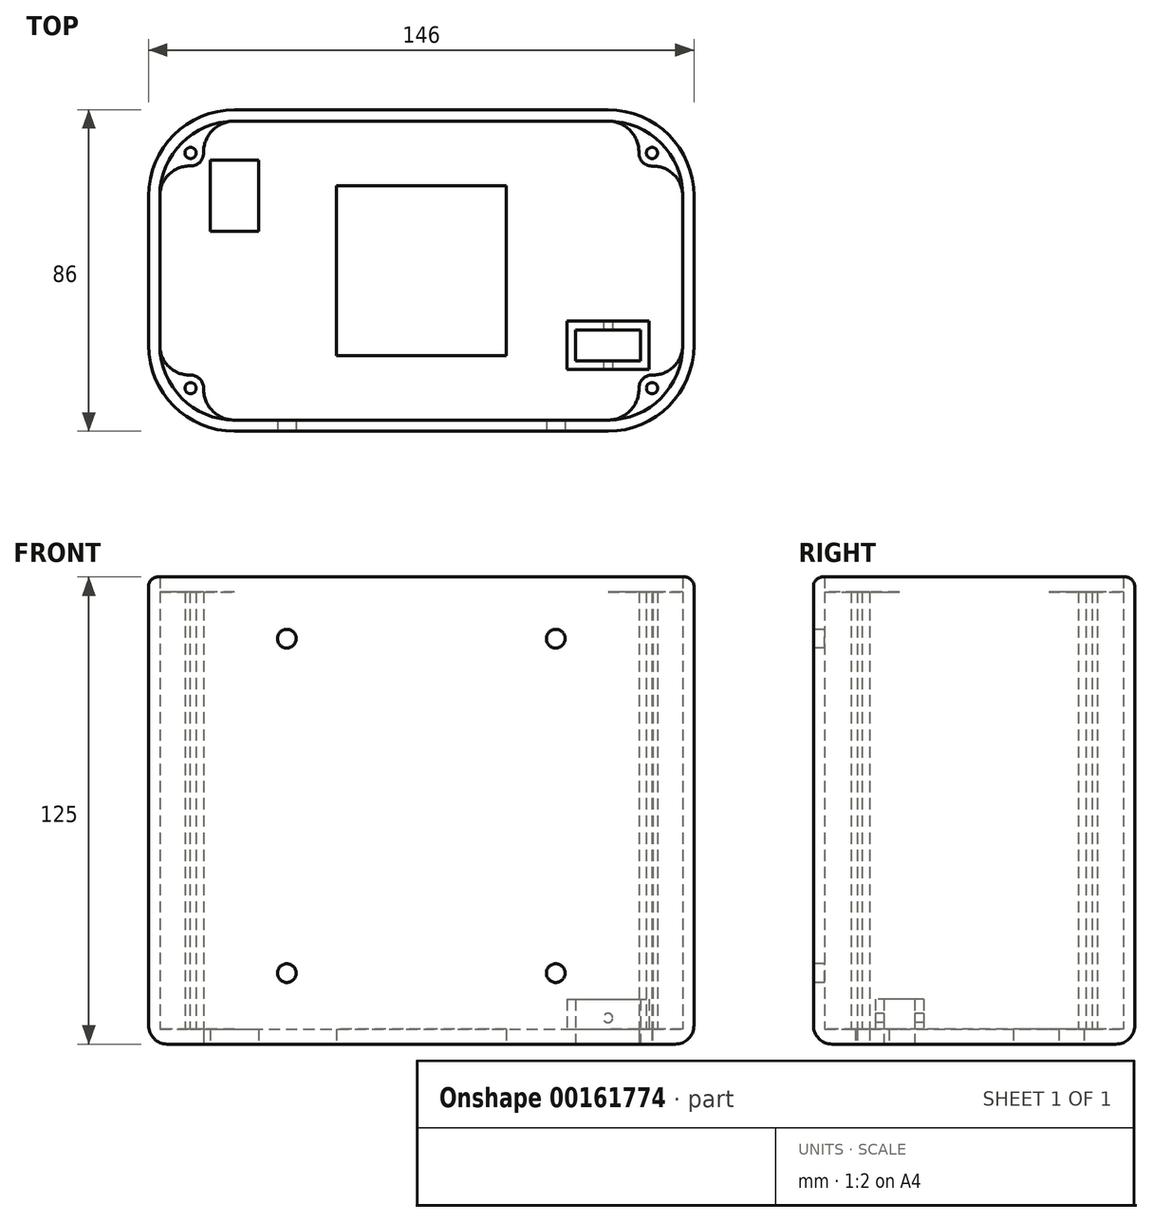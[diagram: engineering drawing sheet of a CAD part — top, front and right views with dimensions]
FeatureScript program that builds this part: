
annotation { "Feature Type Name" : "Feature", "Feature Type Description" : "" }
export const myFeature = defineFeature(function(context is Context, id is Id, definition is map)
    precondition{}
    {
        {
            var Q0;
            Q0=qCreatedBy(makeId("Top.planeOp"),FACE);
            var sketch = newSketch(context, id + "F0", { "sketchPlane" : qUnion([Q0])});
            skPoint(sketch, "E0.middle", {"position": v(5.38, 0.07) * mm});
            skLineSegment(sketch, "E1.left", {"start": v(24.9, 0.52) * mm, "end": v(24.9, -0.25) * mm});
            skLineSegment(sketch, "E2.left", {"start": v(-14.1, 0.52) * mm, "end": v(-14.1, -0.25) * mm});
            skPoint(sketch, "E3.visualSharp", {"position": v(-64.62, 30.07) * mm});
            skPoint(sketch, "E4.visualSharp", {"position": v(75.38, 30.07) * mm});
            skPoint(sketch, "E5.visualSharp", {"position": v(75.38, -29.93) * mm});
            skPoint(sketch, "E6.visualSharp", {"position": v(-64.62, -29.93) * mm});
            skLineSegment(sketch, "E7.bottom", {"start": v(55.38, 40.07) * mm, "end": v(-44.62, 40.07) * mm});
            skLineSegment(sketch, "E7.top", {"start": v(55.38, -39.93) * mm, "end": v(-44.62, -39.93) * mm});
            skLineSegment(sketch, "E7.left", {"start": v(75.38, 20.07) * mm, "end": v(75.38, -19.93) * mm});
            skLineSegment(sketch, "E7.right", {"start": v(-64.62, 20.07) * mm, "end": v(-64.62, -19.93) * mm});
            skPoint(sketch, "E8.visualSharp", {"position": v(-64.62, 40.07) * mm});
            skArc(sketch, "E8.filletArc", {"start": v(-44.62, 40.07) * mm, "mid": v(-58.77, 34.2) * mm, "end": v(-64.62, 20.07) * mm});
            skPoint(sketch, "E9.visualSharp", {"position": v(75.38, 40.07) * mm});
            skArc(sketch, "E9.filletArc", {"start": v(75.38, 20.07) * mm, "mid": v(69.52, 34.2) * mm, "end": v(55.38, 40.07) * mm});
            skPoint(sketch, "E10.visualSharp", {"position": v(75.38, -39.93) * mm});
            skArc(sketch, "E10.filletArc", {"start": v(55.38, -39.93) * mm, "mid": v(69.52, -34.08) * mm, "end": v(75.38, -19.93) * mm});
            skPoint(sketch, "E11.visualSharp", {"position": v(-64.62, -39.93) * mm});
            skArc(sketch, "E11.filletArc", {"start": v(-64.62, -19.93) * mm, "mid": v(-58.77, -34.08) * mm, "end": v(-44.62, -39.93) * mm});
            skLineSegment(sketch, "E12.bottom", {"start": v(-44.62, 44.07) * mm, "end": v(55.38, 44.07) * mm});
            skLineSegment(sketch, "E12.top", {"start": v(-44.62, -43.93) * mm, "end": v(55.38, -43.93) * mm});
            skLineSegment(sketch, "E12.left", {"start": v(-68.62, 20.07) * mm, "end": v(-68.62, -19.93) * mm});
            skLineSegment(sketch, "E12.right", {"start": v(79.38, 20.07) * mm, "end": v(79.38, -19.93) * mm});
            skPoint(sketch, "E13.visualSharp", {"position": v(-68.62, 44.07) * mm});
            skArc(sketch, "E13.filletArc", {"start": v(-44.62, 44.07) * mm, "mid": v(-61.6, 37.04) * mm, "end": v(-68.62, 20.07) * mm});
            skPoint(sketch, "E14.visualSharp", {"position": v(79.38, 44.07) * mm});
            skArc(sketch, "E14.filletArc", {"start": v(79.38, 20.07) * mm, "mid": v(72.35, 37.04) * mm, "end": v(55.38, 44.07) * mm});
            skPoint(sketch, "E15.visualSharp", {"position": v(79.38, -43.93) * mm});
            skArc(sketch, "E15.filletArc", {"start": v(55.38, -43.93) * mm, "mid": v(72.35, -36.9) * mm, "end": v(79.38, -19.93) * mm});
            skPoint(sketch, "E16.visualSharp", {"position": v(-68.62, -43.93) * mm});
            skArc(sketch, "E16.filletArc", {"start": v(-68.62, -19.93) * mm, "mid": v(-61.6, -36.9) * mm, "end": v(-44.62, -43.93) * mm});
            skLineSegment(sketch, "E17.bottom", {"start": v(28.13, 22.82) * mm, "end": v(-17.37, 22.82) * mm});
            skLineSegment(sketch, "E17.top", {"start": v(28.13, -22.68) * mm, "end": v(-17.37, -22.68) * mm});
            skLineSegment(sketch, "E17.left", {"start": v(28.13, 22.82) * mm, "end": v(28.13, -22.68) * mm});
            skLineSegment(sketch, "E17.right", {"start": v(-17.37, 22.82) * mm, "end": v(-17.37, -22.68) * mm});
            skCircle(sketch, "E18", {"center": v(67.15, 31.53) * mm, "radius": 3.5 * mm});
            skCircle(sketch, "E19", {"center": v(67.15, 31.53) * mm, "radius": 1.5 * mm});
            skCircle(sketch, "E20", {"center": v(-56.4, 31.53) * mm, "radius": 3.5 * mm});
            skCircle(sketch, "E21", {"center": v(-56.4, 31.53) * mm, "radius": 1.5 * mm});
            skCircle(sketch, "E22", {"center": v(-56.4, -31.4) * mm, "radius": 3.5 * mm});
            skCircle(sketch, "E23", {"center": v(-56.4, -31.4) * mm, "radius": 1.5 * mm});
            skCircle(sketch, "E24", {"center": v(67.16, -31.4) * mm, "radius": 3.5 * mm});
            skCircle(sketch, "E25", {"center": v(67.16, -31.4) * mm, "radius": 1.5 * mm});
            skLineSegment(sketch, "E26.bottom", {"start": v(48.88, 29.57) * mm, "end": v(61.88, 29.57) * mm});
            skLineSegment(sketch, "E26.top", {"start": v(48.88, 10.57) * mm, "end": v(61.88, 10.57) * mm});
            skLineSegment(sketch, "E26.left", {"start": v(48.88, 29.57) * mm, "end": v(48.88, 10.57) * mm});
            skLineSegment(sketch, "E26.right", {"start": v(61.88, 29.57) * mm, "end": v(61.88, 10.57) * mm});
            skLineSegment(sketch, "E27.bottom", {"start": v(-35.97, -15.78) * mm, "end": v(-53.27, -15.78) * mm});
            skLineSegment(sketch, "E27.top", {"start": v(-35.97, -24.08) * mm, "end": v(-53.27, -24.08) * mm});
            skLineSegment(sketch, "E27.left", {"start": v(-35.97, -15.78) * mm, "end": v(-35.97, -24.08) * mm});
            skLineSegment(sketch, "E27.right", {"start": v(-53.27, -15.78) * mm, "end": v(-53.27, -24.08) * mm});
            skLineSegment(sketch, "E28.bottom", {"start": v(-33.62, -13.43) * mm, "end": v(-55.62, -13.43) * mm});
            skLineSegment(sketch, "E28.top", {"start": v(-33.62, -26.43) * mm, "end": v(-55.62, -26.43) * mm});
            skLineSegment(sketch, "E28.left", {"start": v(-33.62, -13.43) * mm, "end": v(-33.62, -26.43) * mm});
            skLineSegment(sketch, "E28.right", {"start": v(-55.62, -13.43) * mm, "end": v(-55.62, -26.43) * mm});
            skArc(sketch, "E29", {"start": v(75.38, 20.07) * mm, "mid": v(73.03, 25.72) * mm, "end": v(67.36, 28.03) * mm});
            skArc(sketch, "E30", {"start": v(55.38, 40.07) * mm, "mid": v(61.29, 37.58) * mm, "end": v(63.65, 31.62) * mm});
            skArc(sketch, "E31", {"start": v(55.38, -39.93) * mm, "mid": v(61.38, -37.36) * mm, "end": v(63.66, -31.23) * mm});
            skArc(sketch, "E32", {"start": v(67.18, -27.9) * mm, "mid": v(72.96, -25.65) * mm, "end": v(75.38, -19.93) * mm});
            skArc(sketch, "E33", {"start": v(-52.9, -31.22) * mm, "mid": v(-50.63, -37.35) * mm, "end": v(-44.62, -39.93) * mm});
            skArc(sketch, "E34", {"start": v(-64.62, -19.93) * mm, "mid": v(-62.22, -25.63) * mm, "end": v(-56.47, -27.9) * mm});
            skArc(sketch, "E35", {"start": v(-56.64, 28.04) * mm, "mid": v(-62.28, 25.71) * mm, "end": v(-64.62, 20.07) * mm});
            skArc(sketch, "E36", {"start": v(-44.62, 40.07) * mm, "mid": v(-50.52, 37.6) * mm, "end": v(-52.9, 31.67) * mm});
            skLineSegment(sketch, "E37.bottom", {"start": v(-51.12, 29.57) * mm, "end": v(-38.12, 29.57) * mm});
            skLineSegment(sketch, "E37.top", {"start": v(-51.12, 10.57) * mm, "end": v(-38.12, 10.57) * mm});
            skLineSegment(sketch, "E37.left", {"start": v(-51.12, 29.57) * mm, "end": v(-51.12, 10.57) * mm});
            skLineSegment(sketch, "E37.right", {"start": v(-38.12, 29.57) * mm, "end": v(-38.12, 10.57) * mm});
            skLineSegment(sketch, "E38.bottom", {"start": v(46.73, -15.78) * mm, "end": v(64.03, -15.78) * mm});
            skLineSegment(sketch, "E38.top", {"start": v(46.73, -24.08) * mm, "end": v(64.03, -24.08) * mm});
            skLineSegment(sketch, "E38.left", {"start": v(46.73, -15.78) * mm, "end": v(46.73, -24.08) * mm});
            skLineSegment(sketch, "E38.right", {"start": v(64.03, -15.78) * mm, "end": v(64.03, -24.08) * mm});
            skLineSegment(sketch, "E39.bottom", {"start": v(44.38, -13.43) * mm, "end": v(66.38, -13.43) * mm});
            skLineSegment(sketch, "E39.top", {"start": v(44.38, -26.43) * mm, "end": v(66.38, -26.43) * mm});
            skLineSegment(sketch, "E39.left", {"start": v(44.38, -13.43) * mm, "end": v(44.38, -26.43) * mm});
            skLineSegment(sketch, "E39.right", {"start": v(66.38, -13.43) * mm, "end": v(66.38, -26.43) * mm});
            skArc(sketch, "E40.0", {"start": v(78.38, 20.07) * mm, "mid": v(71.64, 36.33) * mm, "end": v(55.38, 43.07) * mm});
            skLineSegment(sketch, "E40.1", {"start": v(78.38, 20.07) * mm, "end": v(78.38, -19.93) * mm});
            skLineSegment(sketch, "E40.2", {"start": v(55.38, 43.07) * mm, "end": v(-44.62, 43.07) * mm});
            skArc(sketch, "E40.3", {"start": v(55.38, -42.93) * mm, "mid": v(71.64, -36.2) * mm, "end": v(78.38, -19.93) * mm});
            skArc(sketch, "E40.4", {"start": v(-44.62, 43.07) * mm, "mid": v(-60.89, 36.33) * mm, "end": v(-67.62, 20.07) * mm});
            skLineSegment(sketch, "E40.5", {"start": v(-67.62, 20.07) * mm, "end": v(-67.62, -19.93) * mm});
            skArc(sketch, "E40.6", {"start": v(-67.62, -19.93) * mm, "mid": v(-60.89, -36.2) * mm, "end": v(-44.62, -42.93) * mm});
            skLineSegment(sketch, "E40.7", {"start": v(55.38, -42.93) * mm, "end": v(-44.62, -42.93) * mm});
            skSolve(sketch);
        }
        {
            var Q0;
            Q0=makeQuery(id+"F0.imprint","IMPRINT",FACE,{"disambiguationData":[TD([[makeQuery(id+"F0.imprint","IMPRINT",EDGE,{"derivedFrom":sQuery(id+"F0.wireOp",EDGE,"E7.bottom")}),1.0]])]});
            var Q1;
            Q1=makeQuery(id+"F0.imprint","IMPRINT",FACE,{"disambiguationData":[TD([[makeQuery(id+"F0.imprint","IMPRINT",EDGE,{"derivedFrom":sQuery(id+"F0.wireOp",EDGE,"E18")}),1.0]])]});
            var Q2;
            Q2=makeQuery(id+"F0.imprint","IMPRINT",FACE,{"disambiguationData":[TD([[makeQuery(id+"F0.imprint","IMPRINT",EDGE,{"derivedFrom":sQuery(id+"F0.wireOp",EDGE,"E19")}),1.0]])]});
            var Q3;
            Q3=makeQuery(id+"F0.imprint","IMPRINT",FACE,{"disambiguationData":[TD([[makeQuery(id+"F0.imprint","IMPRINT",EDGE,{"derivedFrom":sQuery(id+"F0.wireOp",EDGE,"E24")}),1.0]])]});
            var Q4;
            Q4=makeQuery(id+"F0.imprint","IMPRINT",FACE,{"disambiguationData":[TD([[makeQuery(id+"F0.imprint","IMPRINT",EDGE,{"derivedFrom":sQuery(id+"F0.wireOp",EDGE,"E25")}),1.0]])]});
            var Q5;
            Q5=makeQuery(id+"F0.imprint","IMPRINT",FACE,{"disambiguationData":[TD([[makeQuery(id+"F0.imprint","IMPRINT",EDGE,{"derivedFrom":sQuery(id+"F0.wireOp",EDGE,"E22")}),1.0]])]});
            var Q6;
            Q6=makeQuery(id+"F0.imprint","IMPRINT",FACE,{"disambiguationData":[TD([[makeQuery(id+"F0.imprint","IMPRINT",EDGE,{"derivedFrom":sQuery(id+"F0.wireOp",EDGE,"E23")}),1.0]])]});
            var Q7;
            Q7=makeQuery(id+"F0.imprint","IMPRINT",FACE,{"disambiguationData":[TD([[makeQuery(id+"F0.imprint","IMPRINT",EDGE,{"derivedFrom":sQuery(id+"F0.wireOp",EDGE,"E20")}),1.0]])]});
            var Q8;
            Q8=makeQuery(id+"F0.imprint","IMPRINT",FACE,{"disambiguationData":[TD([[makeQuery(id+"F0.imprint","IMPRINT",EDGE,{"derivedFrom":sQuery(id+"F0.wireOp",EDGE,"E21")}),1.0]])]});
            var Q9;
            Q9=makeQuery(id+"F0.imprint","IMPRINT",FACE,{"disambiguationData":[TD([[makeQuery(id+"F0.imprint","IMPRINT",EDGE,{"derivedFrom":sQuery(id+"F0.wireOp",EDGE,"E7.bottom")}),-1.0]])]});
            var Q10;
            Q10=makeQuery(id+"F0.imprint","IMPRINT",FACE,{"disambiguationData":[TD([[makeQuery(id+"F0.imprint","IMPRINT",EDGE,{"derivedFrom":sQuery(id+"F0.wireOp",EDGE,"E8.filletArc")}),1.0]])]});
            var Q11;
            Q11=makeQuery(id+"F0.imprint","IMPRINT",FACE,{"disambiguationData":[TD([[makeQuery(id+"F0.imprint","IMPRINT",EDGE,{"derivedFrom":sQuery(id+"F0.wireOp",EDGE,"E9.filletArc")}),1.0]])]});
            var Q12;
            {var subQ0=sQuery(id+"F0.wireOp",EDGE,"E10.filletArc");Q12=makeQuery(id+"F0.imprint","IMPRINT",FACE,{"disambiguationData":[TD([[makeQuery(id+"F0.imprint","IMPRINT",EDGE,{"derivedFrom":subQ0}),1.0]])]});}
            var Q13;
            {var subQ0=sQuery(id+"F0.wireOp",EDGE,"E11.filletArc");Q13=makeQuery(id+"F0.imprint","IMPRINT",FACE,{"disambiguationData":[TD([[makeQuery(id+"F0.imprint","IMPRINT",EDGE,{"derivedFrom":subQ0}),1.0]])]});}
            var Q14;
            Q14=makeQuery(id+"F0.imprint","IMPRINT",FACE,{"disambiguationData":[TD([[makeQuery(id+"F0.imprint","IMPRINT",EDGE,{"derivedFrom":sQuery(id+"F0.wireOp",EDGE,"E26.bottom")}),-1.0]])]});
            var Q15;
            Q15=makeQuery(id+"F0.imprint","IMPRINT",FACE,{"disambiguationData":[TD([[makeQuery(id+"F0.imprint","IMPRINT",EDGE,{"derivedFrom":sQuery(id+"F0.wireOp",EDGE,"E27.bottom")}),-1.0]])]});
            var Q16;
            Q16=makeQuery(id+"F0.imprint","IMPRINT",FACE,{"disambiguationData":[TD([[makeQuery(id+"F0.imprint","IMPRINT",EDGE,{"derivedFrom":sQuery(id+"F0.wireOp",EDGE,"E27.bottom")}),1.0]])]});
            extrude(context, id + "F1", {"entities" : qUnion([Q0, Q1, Q2, Q3, Q4, Q5, Q6, Q7, Q8, Q9, Q10, Q11, Q12, Q13, Q14, Q15, Q16]), "depth" : 4 * mm});
        }
        {
            var Q0;
            Q0=makeQuery(id+"F0.imprint","IMPRINT",FACE,{"disambiguationData":[TD([[makeQuery(id+"F0.imprint","IMPRINT",EDGE,{"derivedFrom":sQuery(id+"F0.wireOp",EDGE,"E38.bottom")}),1.0]])]});
            extrude(context, id + "F2", {"entities" : qUnion([Q0]), "operationType" : NewBodyOperationType.ADD, "depth" : 12 * mm});
        }
        {
            var Q0;
            Q0=makeQuery(id+"F0.imprint","IMPRINT",FACE,{"disambiguationData":[TD([[makeQuery(id+"F0.imprint","IMPRINT",EDGE,{"derivedFrom":sQuery(id+"F0.wireOp",EDGE,"E8.filletArc")}),1.0]])]});
            var Q1;
            Q1=makeQuery(id+"F0.imprint","IMPRINT",FACE,{"disambiguationData":[TD([[makeQuery(id+"F0.imprint","IMPRINT",EDGE,{"derivedFrom":sQuery(id+"F0.wireOp",EDGE,"E21")}),-1.0]])]});
            var Q2;
            {var subQ0=sQuery(id+"F0.wireOp",EDGE,"E11.filletArc");Q2=makeQuery(id+"F0.imprint","IMPRINT",FACE,{"disambiguationData":[TD([[makeQuery(id+"F0.imprint","IMPRINT",EDGE,{"derivedFrom":subQ0}),1.0]])]});}
            var Q3;
            Q3=makeQuery(id+"F0.imprint","IMPRINT",FACE,{"disambiguationData":[TD([[makeQuery(id+"F0.imprint","IMPRINT",EDGE,{"derivedFrom":sQuery(id+"F0.wireOp",EDGE,"E23")}),-1.0]])]});
            var Q4;
            {var subQ0=sQuery(id+"F0.wireOp",EDGE,"E10.filletArc");Q4=makeQuery(id+"F0.imprint","IMPRINT",FACE,{"disambiguationData":[TD([[makeQuery(id+"F0.imprint","IMPRINT",EDGE,{"derivedFrom":subQ0}),1.0]])]});}
            var Q5;
            Q5=makeQuery(id+"F0.imprint","IMPRINT",FACE,{"disambiguationData":[TD([[makeQuery(id+"F0.imprint","IMPRINT",EDGE,{"derivedFrom":sQuery(id+"F0.wireOp",EDGE,"E25")}),-1.0]])]});
            var Q6;
            Q6=makeQuery(id+"F0.imprint","IMPRINT",FACE,{"disambiguationData":[TD([[makeQuery(id+"F0.imprint","IMPRINT",EDGE,{"derivedFrom":sQuery(id+"F0.wireOp",EDGE,"E9.filletArc")}),1.0]])]});
            var Q7;
            Q7=makeQuery(id+"F0.imprint","IMPRINT",FACE,{"disambiguationData":[TD([[makeQuery(id+"F0.imprint","IMPRINT",EDGE,{"derivedFrom":sQuery(id+"F0.wireOp",EDGE,"E19")}),-1.0]])]});
            extrude(context, id + "F3", {"entities" : qUnion([Q0, Q1, Q2, Q3, Q4, Q5, Q6, Q7]), "operationType" : NewBodyOperationType.ADD, "depth" : 121 * mm});
        }
        {
            var Q0;
            Q0=makeQuery(id+"F0.imprint","IMPRINT",FACE,{"disambiguationData":[TD([[makeQuery(id+"F0.imprint","IMPRINT",EDGE,{"derivedFrom":sQuery(id+"F0.wireOp",EDGE,"E7.bottom")}),-1.0]])]});
            extrude(context, id + "F4", {"entities" : qUnion([Q0]), "operationType" : NewBodyOperationType.ADD, "depth" : 125 * mm});
        }
        {
            var Q0;
            Q0=makeQuery(id+"F1.opExtrude","CAP_EDGE",EDGE,{"disambiguationData":[OSD([sQuery(id+"F0.wireOp",EDGE,"E40.2")])],"isStart":true});
            fillet(context, id + "F5", {"entities" : qUnion([Q0]), "radius" : 5 * mm, "tangentPropagation" : true, "allowEdgeOverflow" : false});
        }
        {
            var Q0;
            Q0=makeQuery(id+"F4.opExtrude","CAP_EDGE",EDGE,{"disambiguationData":[OSD([sQuery(id+"F0.wireOp",EDGE,"E40.2")])],"isStart":false});
            fillet(context, id + "F6", {"entities" : qUnion([Q0]), "radius" : 2.5 * mm, "tangentPropagation" : true, "allowEdgeOverflow" : false});
        }
        {
            var Q0;
            Q0=makeQuery(id+"F2.opExtrude","SWEPT_FACE",FACE,{"disambiguationData":[OSD([sQuery(id+"F0.wireOp",EDGE,"E38.top")])]});
            var sketch = newSketch(context, id + "F7", { "sketchPlane" : qUnion([Q0])});
            skLineSegment(sketch, "E41", {"start": v(-55.38, 0) * mm, "end": v(-55.38, 7) * mm});
            skCircle(sketch, "E42", {"center": v(-55.38, 7) * mm, "radius": 1.25 * mm});
            skSolve(sketch);
        }
        {
            var Q0;
            Q0=makeQuery(id+"F7.imprint","IMPRINT",FACE,{"disambiguationData":[TD([[makeQuery(id+"F7.imprint","IMPRINT",EDGE,{"derivedFrom":sQuery(id+"F7.wireOp",EDGE,"E42")}),1.0]])]});
            extrude(context, id + "F8", {"entities" : qUnion([Q0]), "operationType" : NewBodyOperationType.REMOVE, "endBound" : BoundingType.SYMMETRIC, "depth" : 30 * mm});
        }
        {
            var Q0;
            {var subQ0=sQuery(id+"F0.wireOp",EDGE,"E40.7");Q0=makeQuery(id+"F4.boolean.opBoolean","MERGE",FACE,{"derivedFrom":[makeQuery(id+"F1.opExtrude","SWEPT_FACE",FACE,{"disambiguationData":[OSD([subQ0])]}),makeQuery(id+"F4.opExtrude","SWEPT_FACE",FACE,{"disambiguationData":[OSD([subQ0])]})]});}
            var sketch = newSketch(context, id + "F9", { "sketchPlane" : qUnion([Q0])});
            skLineSegment(sketch, "E43.bottom", {"start": v(-44.62, 122.5) * mm, "end": v(-30.62, 122.5) * mm});
            skLineSegment(sketch, "E43.top", {"start": v(-44.62, 108.5) * mm, "end": v(-30.62, 108.5) * mm});
            skLineSegment(sketch, "E43.left", {"start": v(-44.62, 122.5) * mm, "end": v(-44.62, 108.5) * mm});
            skLineSegment(sketch, "E43.right", {"start": v(-30.62, 122.5) * mm, "end": v(-30.62, 108.5) * mm});
            skLineSegment(sketch, "E44.bottom", {"start": v(-44.62, 5) * mm, "end": v(-30.62, 5) * mm});
            skLineSegment(sketch, "E44.top", {"start": v(-44.62, 19) * mm, "end": v(-30.62, 19) * mm});
            skLineSegment(sketch, "E44.left", {"start": v(-44.62, 5) * mm, "end": v(-44.62, 19) * mm});
            skLineSegment(sketch, "E44.right", {"start": v(-30.62, 5) * mm, "end": v(-30.62, 19) * mm});
            skLineSegment(sketch, "E45.bottom", {"start": v(55.38, 5) * mm, "end": v(41.38, 5) * mm});
            skLineSegment(sketch, "E45.top", {"start": v(55.38, 19) * mm, "end": v(41.38, 19) * mm});
            skLineSegment(sketch, "E45.left", {"start": v(55.38, 5) * mm, "end": v(55.38, 19) * mm});
            skLineSegment(sketch, "E45.right", {"start": v(41.38, 5) * mm, "end": v(41.38, 19) * mm});
            skLineSegment(sketch, "E46.bottom", {"start": v(55.38, 122.5) * mm, "end": v(41.38, 122.5) * mm});
            skLineSegment(sketch, "E46.top", {"start": v(55.38, 108.5) * mm, "end": v(41.38, 108.5) * mm});
            skLineSegment(sketch, "E46.left", {"start": v(55.38, 122.5) * mm, "end": v(55.38, 108.5) * mm});
            skLineSegment(sketch, "E46.right", {"start": v(41.38, 122.5) * mm, "end": v(41.38, 108.5) * mm});
            skCircle(sketch, "E47", {"center": v(-30.62, 108.5) * mm, "radius": 2.5 * mm});
            skCircle(sketch, "E48", {"center": v(41.38, 108.5) * mm, "radius": 2.5 * mm});
            skCircle(sketch, "E49", {"center": v(-30.62, 19) * mm, "radius": 2.5 * mm});
            skCircle(sketch, "E50", {"center": v(41.38, 19) * mm, "radius": 2.5 * mm});
            skSolve(sketch);
        }
        {
            var Q0;
            {var subQ0=sQuery(id+"F9.wireOp",EDGE,"E43.right");var subQ1=sQuery(id+"F9.wireOp",EDGE,"E43.top");var subQ2=makeQuery(id+"F9.imprint","INTERSECT",VERTEX,{"derivedFrom":[subQ1,subQ0]});Q0=makeQuery(id+"F9.imprint","IMPRINT",FACE,{"disambiguationData":[TD([[makeQuery(id+"F9.imprint","IMPRINT",EDGE,{"disambiguationData":[TD([[subQ2,1.0]])],"derivedFrom":subQ1}),1.0]])]});}
            var Q1;
            {var subQ0=sQuery(id+"F9.wireOp",EDGE,"E43.right");var subQ1=sQuery(id+"F9.wireOp",EDGE,"E43.top");var subQ2=makeQuery(id+"F9.imprint","INTERSECT",VERTEX,{"derivedFrom":[subQ1,subQ0]});Q1=makeQuery(id+"F9.imprint","IMPRINT",FACE,{"disambiguationData":[TD([[makeQuery(id+"F9.imprint","IMPRINT",EDGE,{"disambiguationData":[TD([[subQ2,1.0]])],"derivedFrom":subQ1}),-1.0]])]});}
            var Q2;
            {var subQ0=sQuery(id+"F9.wireOp",EDGE,"E44.right");var subQ1=sQuery(id+"F9.wireOp",EDGE,"E44.top");var subQ2=makeQuery(id+"F9.imprint","INTERSECT",VERTEX,{"derivedFrom":[subQ1,subQ0]});Q2=makeQuery(id+"F9.imprint","IMPRINT",FACE,{"disambiguationData":[TD([[makeQuery(id+"F9.imprint","IMPRINT",EDGE,{"disambiguationData":[TD([[subQ2,1.0]])],"derivedFrom":subQ1}),-1.0]])]});}
            var Q3;
            {var subQ0=sQuery(id+"F9.wireOp",EDGE,"E44.right");var subQ1=sQuery(id+"F9.wireOp",EDGE,"E44.top");var subQ2=makeQuery(id+"F9.imprint","INTERSECT",VERTEX,{"derivedFrom":[subQ1,subQ0]});Q3=makeQuery(id+"F9.imprint","IMPRINT",FACE,{"disambiguationData":[TD([[makeQuery(id+"F9.imprint","IMPRINT",EDGE,{"disambiguationData":[TD([[subQ2,1.0]])],"derivedFrom":subQ1}),1.0]])]});}
            var Q4;
            {var subQ0=sQuery(id+"F9.wireOp",EDGE,"E45.right");var subQ1=sQuery(id+"F9.wireOp",EDGE,"E45.top");var subQ2=makeQuery(id+"F9.imprint","INTERSECT",VERTEX,{"derivedFrom":[subQ1,subQ0]});Q4=makeQuery(id+"F9.imprint","IMPRINT",FACE,{"disambiguationData":[TD([[makeQuery(id+"F9.imprint","IMPRINT",EDGE,{"disambiguationData":[TD([[subQ2,1.0]])],"derivedFrom":subQ1}),-1.0]])]});}
            var Q5;
            {var subQ0=sQuery(id+"F9.wireOp",EDGE,"E45.right");var subQ1=sQuery(id+"F9.wireOp",EDGE,"E45.top");var subQ2=makeQuery(id+"F9.imprint","INTERSECT",VERTEX,{"derivedFrom":[subQ1,subQ0]});Q5=makeQuery(id+"F9.imprint","IMPRINT",FACE,{"disambiguationData":[TD([[makeQuery(id+"F9.imprint","IMPRINT",EDGE,{"disambiguationData":[TD([[subQ2,1.0]])],"derivedFrom":subQ1}),1.0]])]});}
            var Q6;
            {var subQ0=sQuery(id+"F9.wireOp",EDGE,"E46.right");var subQ1=sQuery(id+"F9.wireOp",EDGE,"E46.top");var subQ2=makeQuery(id+"F9.imprint","INTERSECT",VERTEX,{"derivedFrom":[subQ1,subQ0]});Q6=makeQuery(id+"F9.imprint","IMPRINT",FACE,{"disambiguationData":[TD([[makeQuery(id+"F9.imprint","IMPRINT",EDGE,{"disambiguationData":[TD([[subQ2,1.0]])],"derivedFrom":subQ1}),-1.0]])]});}
            var Q7;
            {var subQ0=sQuery(id+"F9.wireOp",EDGE,"E46.right");var subQ1=sQuery(id+"F9.wireOp",EDGE,"E46.top");var subQ2=makeQuery(id+"F9.imprint","INTERSECT",VERTEX,{"derivedFrom":[subQ1,subQ0]});Q7=makeQuery(id+"F9.imprint","IMPRINT",FACE,{"disambiguationData":[TD([[makeQuery(id+"F9.imprint","IMPRINT",EDGE,{"disambiguationData":[TD([[subQ2,1.0]])],"derivedFrom":subQ1}),1.0]])]});}
            extrude(context, id + "F10", {"entities" : qUnion([Q0, Q1, Q2, Q3, Q4, Q5, Q6, Q7]), "operationType" : NewBodyOperationType.REMOVE, "oppositeDirection" : true, "depth" : 3.5 * mm});
        }
    });
